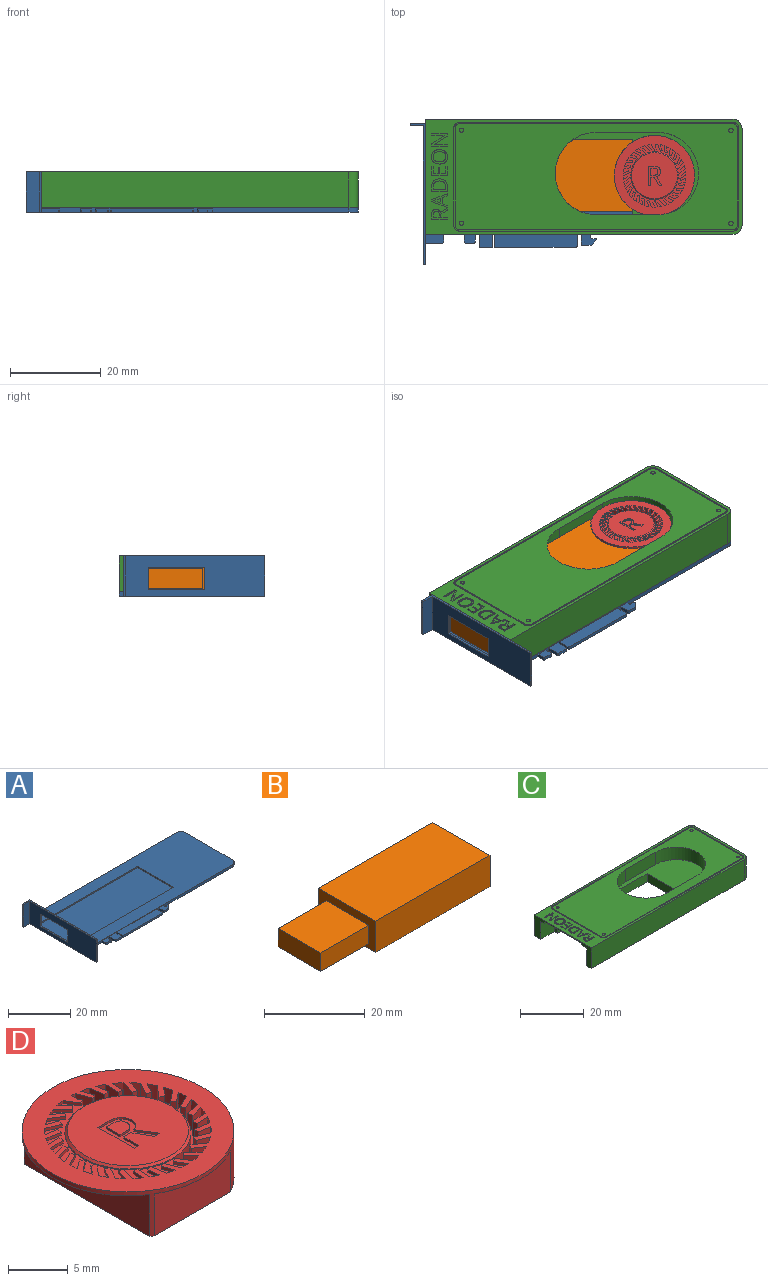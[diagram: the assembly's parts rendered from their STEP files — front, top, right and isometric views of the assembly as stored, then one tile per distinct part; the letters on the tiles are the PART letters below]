
ASSEMBLY  parts=4 mates=3
PART A: 54 faces, bbox 73.4x32.1x8.9 mm
  f0: plane 31.16x8.92mm, normal (1,0,0), area 199.6mm2, adj f2,f6,f7,f21,f22,f39,f40,f43
  f1: plane 30.69x8.92mm, normal (-1,0,0), area 212.9mm2, adj f7,f40,f41,f43,f50,f51,f52,f53
  f2: plane 70x25.41mm, normal (0,0,1), area 1021.4mm2, adj f0,f3,f4,f5,f6,f44,f45,f46
  f3: plane 1x0.96mm, normal (-1,0,0), area 1mm2, adj f2,f5,f7,f39
  f4: plane 21.41x1mm, normal (1,0,0), area 21.4mm2, adj f2,f7,f44,f45
  f5: plane 68x1mm, normal (0,1,0), area 68mm2, adj f2,f3,f7,f44
  f6: plane 68x1mm, normal (0,-1,0), area 46.8mm2, adj f0,f2,f7,f8,f9,f11,f12,f13
  f7: plane 73.36x32.12mm, normal (0,0,-1), area 1872.4mm2, adj f0,f1,f3,f4,f5,f6,f8,f9
  f8: plane 2.68x0.72mm, normal (-1,0,0), area 1.9mm2, adj f6,f7,f11,f37
  f9: plane 2.68x0.72mm, normal (1,0,0), area 1.9mm2, adj f6,f7,f11,f38
  f10: plane 17.82x0.72mm, normal (0,-1,0), area 12.8mm2, adj f7,f11,f37,f38
  f11: plane 18.22x2.88mm, normal (0,0,1), area 52.4mm2, adj f6,f8,f9,f10,f37,f38
  f12: plane 2.68x0.72mm, normal (-1,0,0), area 1.9mm2, adj f6,f7,f15,f36
  f13: plane 2.68x0.72mm, normal (1,0,0), area 1.9mm2, adj f6,f7,f15,f35
  f14: plane 2.48x0.72mm, normal (0,-1,0), area 1.8mm2, adj f7,f15,f35,f36
  f15: plane 2.88x2.88mm, normal (0,0,1), area 8.3mm2, adj f6,f12,f13,f14,f35,f36
  f16: plane 1.72x0.72mm, normal (-1,0,0), area 1.2mm2, adj f6,f7,f19,f33
  f17: plane 1.72x0.72mm, normal (1,0,0), area 1.2mm2, adj f6,f7,f19,f34
  f18: plane 2x0.72mm, normal (0,-1,0), area 1.4mm2, adj f7,f19,f33,f34
  f19: plane 2.4x1.92mm, normal (0,0,1), area 4.6mm2, adj f6,f16,f17,f18,f33,f34
  f20: plane 1.72x0.72mm, normal (1,0,0), area 1.2mm2, adj f6,f7,f22,f32
  f21: plane 3.88x0.72mm, normal (0,-1,0), area 2.8mm2, adj f0,f7,f22,f32
  f22: plane 4.08x1.92mm, normal (0,0,1), area 7.8mm2, adj f0,f6,f20,f21,f32
  f23: plane 2.2x0.72mm, normal (-1,0,0), area 1.6mm2, adj f6,f7,f28,f31
  f24: plane 0.72x0.36mm, normal (1,0,0), area 0.3mm2, adj f6,f7,f28,f30
  f25: plane 0.84x0.72mm, normal (0,1,0), area 0.6mm2, adj f7,f26,f28,f30
  f26: plane 0.72x0.24mm, normal (1,0,0), area 0.2mm2, adj f7,f25,f28,f29
  f27: plane 1.96x0.72mm, normal (0,-1,0), area 1.4mm2, adj f7,f28,f29,f31
  f28: plane 3.36x2.4mm, normal (0,0,1), area 6mm2, adj f6,f23,f24,f25,f26,f27,f29,f30
  f29: plane 1.2x1.2mm, normal (0.71,-0.71,0), area 1.2mm2, adj f7,f26,f27,f28
  f30: cylinder r=0.6mm len=0.72mm, axis (0,0,1), area 0.7mm2, adj f7,f24,f25,f28
  f31: cylinder r=0.2mm len=0.72mm, axis (0,0,-1), area 0.2mm2, adj f7,f23,f27,f28
  f32: cylinder r=0.2mm len=0.72mm, axis (0,0,1), area 0.2mm2, adj f7,f20,f21,f22
  f33: cylinder r=0.2mm len=0.72mm, axis (0,0,-1), area 0.2mm2, adj f7,f16,f18,f19
  f34: cylinder r=0.2mm len=0.72mm, axis (0,0,1), area 0.2mm2, adj f7,f17,f18,f19
  f35: cylinder r=0.2mm len=0.72mm, axis (0,0,1), area 0.2mm2, adj f7,f13,f14,f15
  f36: cylinder r=0.2mm len=0.72mm, axis (0,0,-1), area 0.2mm2, adj f7,f12,f14,f15
  f37: cylinder r=0.2mm len=0.72mm, axis (0,0,-1), area 0.2mm2, adj f7,f8,f10,f11
  f38: cylinder r=0.2mm len=0.72mm, axis (0,0,1), area 0.2mm2, adj f7,f9,f10,f11
  f39: plane 8.92x3.36mm, normal (0,1,0), area 29.9mm2, adj f0,f3,f7,f42,f43
  f40: plane 8.92x0.48mm, normal (0,-1,0), area 4.3mm2, adj f0,f1,f7,f43
  f41: plane 8.92x2.88mm, normal (0,-1,0), area 25.7mm2, adj f1,f7,f42,f43
  f42: plane 8.92x0.48mm, normal (-1,0,0), area 4.3mm2, adj f7,f39,f41,f43
  f43: plane 31.16x3.36mm, normal (0,0,1), area 16.3mm2, adj f0,f1,f39,f40,f41,f42
  f44: cylinder r=2mm len=2mm, axis (0,0,1), area 3.1mm2, adj f2,f4,f5,f7
  f45: cylinder r=2mm len=2mm, axis (0,0,-1), area 3.1mm2, adj f2,f4,f6,f7
  f46: plane 45.8x0.5mm, normal (0,-1,0), area 22.9mm2, adj f0,f2,f48,f49
  f47: plane 45.8x0.5mm, normal (0,1,0), area 22.9mm2, adj f0,f2,f48,f49
  f48: plane 16.5x0.5mm, normal (-1,0,0), area 8.2mm2, adj f2,f46,f47,f49
  f49: plane 45.8x16.5mm, normal (0,0,1), area 755.7mm2, adj f0,f46,f47,f48
  f50: plane 4.9x0.48mm, normal (0,1,0), area 2.3mm2, adj f0,f1,f51,f53
  f51: plane 12.4x0.48mm, normal (0,0,-1), area 5.9mm2, adj f0,f1,f50,f52
  f52: plane 4.9x0.48mm, normal (0,-1,0), area 2.3mm2, adj f0,f1,f51,f53
  f53: plane 12.4x0.48mm, normal (0,0,1), area 5.9mm2, adj f0,f1,f50,f52
PART B: 11 faces, bbox 45.5x16x7.6 mm
  f0: plane 16x7.6mm, normal (1,0,0), area 121.6mm2, adj f1,f3,f4,f5
  f1: plane 32x7.6mm, normal (0,1,0), area 243.2mm2, adj f0,f2,f4,f5
  f2: plane 16x7.6mm, normal (-1,0,0), area 67.6mm2, adj f1,f3,f4,f5,f6,f7,f8,f9
  f3: plane 32x7.6mm, normal (0,-1,0), area 243.2mm2, adj f0,f2,f4,f5
  f4: plane 32x16mm, normal (0,0,1), area 512mm2, adj f0,f1,f2,f3
  f5: plane 32x16mm, normal (0,0,-1), area 512mm2, adj f0,f1,f2,f3
  f6: plane 13.5x4.5mm, normal (0,-1,0), area 60.7mm2, adj f2,f7,f9,f10
  f7: plane 13.5x12mm, normal (0,0,1), area 162mm2, adj f2,f6,f8,f10
  f8: plane 13.5x4.5mm, normal (0,1,0), area 60.7mm2, adj f2,f7,f9,f10
  f9: plane 13.5x12mm, normal (0,0,-1), area 162mm2, adj f2,f6,f8,f10
  f10: plane 12x4.5mm, normal (-1,0,0), area 54mm2, adj f6,f7,f8,f9
PART C: 149 faces, bbox 70x25.4x7.9 mm
  f0: plane 62.41x23.4mm, normal (0,0,1), area 950mm2, adj f19,f20,f21,f22,f23,f24,f25,f26
  f1: plane 16.5x3.12mm, normal (-1,0,0), area 51.5mm2, adj f2,f141,f142,f148
  f2: plane 70x25.41mm, normal (0,0,-1), area 997.9mm2, adj f1,f4,f5,f7,f8,f9,f10,f11
  f3: plane 6x1.46mm, normal (0,0,-1), area 8.7mm2, adj f4,f5,f138,f141
  f4: plane 6.92x1.46mm, normal (-1,0,0), area 10.1mm2, adj f2,f3,f138,f141
  f5: plane 25.41x7.92mm, normal (-1,0,0), area 50.4mm2, adj f2,f3,f6,f8,f9,f137,f138,f139
  f6: plane 70x25.41mm, normal (0,0,1), area 231.5mm2, adj f5,f7,f8,f9,f10,f11,f12,f13
  f7: plane 21.41x7.92mm, normal (1,0,0), area 169.5mm2, adj f2,f6,f10,f11
  f8: plane 68x7.92mm, normal (0,1,0), area 538.4mm2, adj f2,f5,f6,f10
  f9: plane 68x7.92mm, normal (0,-1,0), area 538.4mm2, adj f2,f5,f6,f11
  f10: cylinder r=2mm len=7.92mm, axis (0,0,1), area 24.9mm2, adj f2,f6,f7,f8
  f11: cylinder r=2mm len=7.92mm, axis (0,0,-1), area 24.9mm2, adj f2,f6,f7,f9
  f12: plane 21.41x0.1mm, normal (-1,0,0), area 2.1mm2, adj f6,f13,f27,f28
  f13: cylinder r=1.29mm len=1.29mm, axis (0,0,1), area 0.2mm2, adj f6,f12,f14,f28
  f14: plane 60.42x0.1mm, normal (0,-1,0), area 6mm2, adj f6,f13,f15,f28
  f15: cylinder r=1.29mm len=1.29mm, axis (0,0,1), area 0.2mm2, adj f6,f14,f16,f28
  f16: plane 21.41x0.1mm, normal (1,0,0), area 2.1mm2, adj f6,f15,f17,f28
  f17: cylinder r=1.29mm len=1.29mm, axis (0,0,1), area 0.2mm2, adj f6,f16,f18,f28
  f18: plane 60.42x0.1mm, normal (0,1,0), area 6mm2, adj f6,f17,f27,f28
  f19: cylinder r=0.99mm len=0.99mm, axis (0,0,1), area 0.2mm2, adj f0,f20,f26,f28
  f20: plane 21.41x0.1mm, normal (1,0,0), area 2.1mm2, adj f0,f19,f21,f28
  f21: cylinder r=0.99mm len=0.99mm, axis (0,0,1), area 0.2mm2, adj f0,f20,f22,f28
  f22: plane 60.42x0.1mm, normal (0,-1,0), area 6mm2, adj f0,f21,f23,f28
  f23: cylinder r=0.99mm len=0.99mm, axis (0,0,1), area 0.2mm2, adj f0,f22,f24,f28
  f24: plane 21.41x0.1mm, normal (-1,0,0), area 2.1mm2, adj f0,f23,f25,f28
  f25: cylinder r=0.99mm len=0.99mm, axis (0,0,1), area 0.2mm2, adj f0,f24,f26,f28
  f26: plane 60.42x0.1mm, normal (0,1,0), area 6mm2, adj f0,f19,f25,f28
  f27: cylinder r=1.29mm len=1.29mm, axis (0,0,1), area 0.2mm2, adj f6,f12,f18,f28
  f28: plane 63.01x24mm, normal (0,0,1), area 51.3mm2, adj f12,f13,f14,f15,f16,f17,f18,f19
  f29: cylinder r=0.48mm len=0.96mm, axis (0,0,1), area 0.3mm2, adj f0,f30
  f30: plane 0.96x0.96mm, normal (0,0,1), area 0.7mm2, adj f29
  f31: cylinder r=0.48mm len=0.96mm, axis (0,0,1), area 0.3mm2, adj f0,f32
  f32: plane 0.96x0.96mm, normal (0,0,1), area 0.7mm2, adj f31
  f33: cylinder r=0.48mm len=0.96mm, axis (0,0,1), area 0.3mm2, adj f0,f34
  f34: plane 0.96x0.96mm, normal (0,0,1), area 0.7mm2, adj f33
  f35: cylinder r=0.48mm len=0.96mm, axis (0,0,1), area 0.3mm2, adj f0,f36
  f36: plane 0.96x0.96mm, normal (0,0,1), area 0.7mm2, adj f35
  f37: plane 1.93x0.3mm, normal (-1,0,0), area 0.6mm2, adj f6,f38,f48,f49
  f38: plane 0.38x0.3mm, normal (0,-1,0), area 0.1mm2, adj f6,f37,f39,f49
  f39: plane 1.5x0.3mm, normal (1,0,0), area 0.4mm2, adj f6,f38,f40,f49
  f40: plane 1.24x0.3mm, normal (0,-1,0), area 0.4mm2, adj f6,f39,f41,f49
  f41: plane 1.41x0.3mm, normal (-1,0,0), area 0.4mm2, adj f6,f40,f42,f49
  f42: plane 0.38x0.3mm, normal (0,-1,0), area 0.1mm2, adj f6,f41,f43,f49
  f43: plane 1.41x0.3mm, normal (1,0,0), area 0.4mm2, adj f6,f42,f44,f49
  f44: plane 1.08x0.3mm, normal (0,-1,0), area 0.3mm2, adj f6,f43,f45,f49
  f45: plane 1.5x0.3mm, normal (-1,0,0), area 0.4mm2, adj f6,f44,f46,f49
  f46: plane 0.38x0.3mm, normal (0,-1,0), area 0.1mm2, adj f6,f45,f47,f49
  f47: plane 1.93x0.3mm, normal (1,0,0), area 0.6mm2, adj f6,f46,f48,f49
  f48: plane 3.46x0.3mm, normal (0,1,0), area 1mm2, adj f6,f37,f47,f49
  f49: plane 3.46x1.93mm, normal (0,0,1), area 3.2mm2, adj f37,f38,f39,f40,f41,f42,f43,f44
  f50: extruded ~1.05x0.3mm, area 0.3mm2, adj f51,f65,f66,f134
  f51: extruded ~1.04x0.3mm, area 0.3mm2, adj f50,f52,f66,f134
  f52: extruded ~0.85x0.36mm, area 0.3mm2, adj f51,f53,f66,f134
  f53: extruded ~0.84x0.35mm, area 0.3mm2, adj f52,f54,f66,f134
  f54: extruded ~1.04x0.3mm, area 0.3mm2, adj f53,f55,f66,f134
  f55: extruded ~1.05x0.3mm, area 0.3mm2, adj f54,f56,f66,f134
  f56: extruded ~0.85x0.36mm, area 0.3mm2, adj f55,f65,f66,f134
  f57: extruded ~1.31x0.42mm, area 0.4mm2, adj f6,f58,f64,f66
  f58: extruded ~1.31x0.42mm, area 0.4mm2, adj f6,f57,f59,f66
  f59: extruded ~1.17x0.47mm, area 0.4mm2, adj f6,f58,f60,f66
  f60: extruded ~1.19x0.47mm, area 0.4mm2, adj f6,f59,f61,f66
  f61: extruded ~1.31x0.42mm, area 0.4mm2, adj f6,f60,f62,f66
  f62: extruded ~1.32x0.42mm, area 0.4mm2, adj f6,f61,f63,f66
  f63: extruded ~1.18x0.47mm, area 0.4mm2, adj f6,f62,f64,f66
  f64: extruded ~1.18x0.48mm, area 0.4mm2, adj f6,f57,f63,f66
  f65: extruded ~0.85x0.36mm, area 0.3mm2, adj f50,f56,f66,f134
  f66: plane 3.56x3.19mm, normal (0,0,1), area 4mm2, adj f50,f51,f52,f53,f54,f55,f56,f57
  f67: plane 0.51x0.3mm, normal (-1,0,0), area 0.2mm2, adj f6,f68,f84,f85
  f68: plane 3.46x0.3mm, normal (0,-1,0), area 1mm2, adj f6,f67,f69,f85
  f69: plane 0.41x0.3mm, normal (1,0,0), area 0.1mm2, adj f6,f68,f70,f85
  f70: plane 1.95x0.3mm, normal (0,1,0), area 0.6mm2, adj f6,f69,f71,f85
  f71: extruded ~0.51x0.3mm, area 0.2mm2, adj f6,f70,f72,f85
  f72: extruded ~0.41x0.3mm, area 0.1mm2, adj f6,f71,f73,f85
  f73: plane 0.3x0.02mm, normal (1,0,0), area 0mm2, adj f6,f72,f74,f85
  f74: plane 0.94x0.6mm, normal (0.54,-0.84,0), area 0.3mm2, adj f6,f73,f75,f85
  f75: plane 1.76x1.14mm, normal (0.54,-0.84,0), area 0.6mm2, adj f6,f74,f76,f85
  f76: plane 0.3x0.17mm, normal (0.53,-0.85,0), area 0.1mm2, adj f6,f75,f77,f85
  f77: plane 0.5x0.3mm, normal (1,0,0), area 0.2mm2, adj f6,f76,f78,f85
  f78: plane 3.46x0.3mm, normal (0,1,0), area 1mm2, adj f6,f77,f79,f85
  f79: plane 0.4x0.3mm, normal (-1,0,0), area 0.1mm2, adj f6,f78,f80,f85
  f80: plane 1.93x0.3mm, normal (0,-1,0), area 0.6mm2, adj f6,f79,f81,f85
  f81: extruded ~0.75x0.3mm, area 0.2mm2, adj f6,f80,f82,f85
  f82: plane 0.3x0.19mm, normal (0.06,-1,0), area 0.1mm2, adj f6,f81,f83,f85
  f83: plane 0.3x0.02mm, normal (-1,0,0), area 0mm2, adj f6,f82,f84,f85
  f84: plane 2.87x1.85mm, normal (-0.54,0.84,0), area 1mm2, adj f6,f67,f83,f85
  f85: plane 3.46x2.74mm, normal (0,0,1), area 4.3mm2, adj f67,f68,f69,f70,f71,f72,f73,f74
  f86: plane 1.43x0.3mm, normal (0,-1,0), area 0.4mm2, adj f6,f87,f103,f104
  f87: plane 0.69x0.3mm, normal (-1,0,0), area 0.2mm2, adj f6,f86,f88,f104
  f88: plane 1.43x0.84mm, normal (-0.51,0.86,0), area 0.5mm2, adj f6,f87,f89,f104
  f89: plane 0.51x0.3mm, normal (-1,0,0), area 0.2mm2, adj f6,f88,f90,f104
  f90: plane 1.55x0.95mm, normal (0.52,-0.85,0), area 0.5mm2, adj f6,f89,f91,f104
  f91: extruded ~0.93x0.69mm, area 0.4mm2, adj f6,f90,f92,f104
  f92: extruded ~0.74x0.31mm, area 0.2mm2, adj f6,f91,f93,f104
  f93: extruded ~0.95x0.3mm, area 0.3mm2, adj f6,f92,f94,f104
  f94: plane 0.95x0.3mm, normal (1,0,0), area 0.3mm2, adj f6,f93,f95,f104
  f95: plane 3.46x0.3mm, normal (0,1,0), area 1mm2, adj f6,f94,f103,f104
  f96: plane 0.52x0.3mm, normal (1,0,0), area 0.2mm2, adj f97,f102,f104,f105
  f97: plane 1.29x0.3mm, normal (0,-1,0), area 0.4mm2, adj f96,f98,f104,f105
  f98: plane 0.49x0.3mm, normal (-1,0,0), area 0.1mm2, adj f97,f99,f104,f105
  f99: extruded ~0.64x0.3mm, area 0.2mm2, adj f98,f100,f104,f105
  f100: extruded ~0.48x0.3mm, area 0.2mm2, adj f99,f101,f104,f105
  f101: extruded ~0.49x0.3mm, area 0.2mm2, adj f100,f102,f104,f105
  f102: extruded ~0.62x0.3mm, area 0.2mm2, adj f96,f101,f104,f105
  f103: plane 0.44x0.3mm, normal (-1,0,0), area 0.1mm2, adj f6,f86,f95,f104
  f104: plane 3.46x2.47mm, normal (0,0,1), area 3.8mm2, adj f86,f87,f88,f89,f90,f91,f92,f93
  f105: plane 1.33x1.29mm, normal (0,0,1), area 1.5mm2, adj f96,f97,f98,f99,f100,f101,f102
  f106: plane 1.05x0.39mm, normal (-0.35,0.94,0), area 0.3mm2, adj f107,f118,f119,f135
  f107: plane 1.1x0.3mm, normal (1,0,0), area 0.3mm2, adj f106,f108,f119,f135
  f108: plane 1.05x0.39mm, normal (-0.35,-0.94,0), area 0.3mm2, adj f107,f109,f119,f135
  f109: extruded ~0.52x0.3mm, area 0.2mm2, adj f108,f118,f119,f135
  f110: plane 1.07x0.42mm, normal (-0.36,0.93,0), area 0.3mm2, adj f6,f111,f117,f119
  f111: plane 0.45x0.3mm, normal (-1,0,0), area 0.1mm2, adj f6,f110,f112,f119
  f112: plane 3.47x1.35mm, normal (0.36,-0.93,0), area 1.1mm2, adj f6,f111,f113,f119
  f113: plane 0.39x0.3mm, normal (1,0,0), area 0.1mm2, adj f6,f112,f114,f119
  f114: plane 3.47x1.35mm, normal (0.36,0.93,0), area 1.1mm2, adj f6,f113,f115,f119
  f115: plane 0.44x0.3mm, normal (-1,0,0), area 0.1mm2, adj f6,f114,f116,f119
  f116: plane 1.07x0.41mm, normal (-0.36,-0.93,0), area 0.3mm2, adj f6,f115,f117,f119
  f117: plane 1.37x0.3mm, normal (-1,0,0), area 0.4mm2, adj f6,f110,f116,f119
  f118: plane 0.52x0.3mm, normal (-0.3,0.95,0), area 0.2mm2, adj f106,f109,f119,f135
  f119: plane 3.47x3.09mm, normal (0,0,1), area 3.3mm2, adj f106,f107,f108,f109,f110,f111,f112,f113
  f120: extruded ~1x0.33mm, area 0.3mm2, adj f121,f132,f133,f136
  f121: extruded ~1.41x1.37mm, area 0.7mm2, adj f120,f122,f133,f136
  f122: plane 0.47x0.3mm, normal (1,0,0), area 0.1mm2, adj f121,f123,f133,f136
  f123: plane 2.71x0.3mm, normal (0,-1,0), area 0.8mm2, adj f122,f124,f133,f136
  f124: plane 0.57x0.3mm, normal (-1,0,0), area 0.2mm2, adj f123,f132,f133,f136
  f125: extruded ~1.31x0.47mm, area 0.4mm2, adj f6,f126,f131,f133
  f126: extruded ~1.25x0.45mm, area 0.4mm2, adj f6,f125,f127,f133
  f127: extruded ~1.26x0.44mm, area 0.4mm2, adj f6,f126,f128,f133
  f128: plane 1.06x0.3mm, normal (1,0,0), area 0.3mm2, adj f6,f127,f129,f133
  f129: plane 3.46x0.3mm, normal (0,1,0), area 1mm2, adj f6,f128,f130,f133
  f130: plane 0.96x0.3mm, normal (-1,0,0), area 0.3mm2, adj f6,f129,f131,f133
  f131: extruded ~1.34x0.45mm, area 0.4mm2, adj f6,f125,f130,f133
  f132: extruded ~0.98x0.34mm, area 0.3mm2, adj f120,f124,f133,f136
  f133: plane 3.46x2.77mm, normal (0,0,1), area 4mm2, adj f120,f121,f122,f123,f124,f125,f126,f127
  f134: plane 2.8x2.27mm, normal (0,0,1), area 5.3mm2, adj f50,f51,f52,f53,f54,f55,f56,f65
  f135: plane 1.57x1.1mm, normal (0,0,1), area 0.8mm2, adj f106,f107,f108,f109,f118
  f136: plane 2.71x1.88mm, normal (0,0,1), area 4.5mm2, adj f120,f121,f122,f123,f124,f132
  f137: plane 6x2.46mm, normal (0,0,-1), area 14.7mm2, adj f5,f139,f140,f142
  f138: plane 6.92x6mm, normal (0,-1,0), area 41.5mm2, adj f2,f3,f4,f5
  f139: plane 6.92x6mm, normal (0,1,0), area 41.5mm2, adj f2,f5,f137,f140
  f140: plane 6.92x2.46mm, normal (-1,0,0), area 17mm2, adj f2,f137,f139,f142
  f141: plane 45.8x7.5mm, normal (0,-1,0), area 244.6mm2, adj f1,f2,f3,f4,f5,f143,f145,f148
  f142: plane 45.8x7.5mm, normal (0,1,0), area 260mm2, adj f1,f2,f5,f137,f140,f143,f145,f148
  f143: plane 36.22x16.5mm, normal (0,0,-1), area 499.1mm2, adj f5,f141,f142,f145
  f144: plane 13.49x4.79mm, normal (0,-1,0), area 64.7mm2, adj f0,f145,f147,f148
  f145: cylinder r=9.11mm len=18.22mm, axis (0,0,1), area 42.8mm2, adj f0,f141,f142,f143,f144,f146,f148
  f146: plane 13.49x4.79mm, normal (0,1,0), area 64.7mm2, adj f0,f145,f147,f148
  f147: cylinder r=9.11mm len=18.22mm, axis (0,0,1), area 137.2mm2, adj f0,f144,f146,f148
  f148: plane 27.73x18.22mm, normal (0,0,1), area 250mm2, adj f1,f141,f142,f144,f145,f146,f147
PART D: 157 faces, bbox 17.7x17.7x4.7 mm
  f0: plane 10.15x10.15mm, normal (0,0,1), area 72.7mm2, adj f136,f143,f144,f145,f146,f147,f148,f149
  f1: cylinder r=8.87mm len=17.74mm, axis (0,0,-1), area 105.5mm2, adj f2,f3,f4,f5,f6,f7,f8,f9
  f2: plane 15.28x13.74mm, normal (0,0,-1), area 190.4mm2, adj f1,f4,f6,f9
  f3: plane 17.74x17.74mm, normal (0,0,1), area 117.1mm2, adj f1,f10,f11,f12,f13,f14,f15,f16
  f4: plane 9.01x4.29mm, normal (0,1,0), area 38.6mm2, adj f1,f2,f5
  f5: plane 9.01x1.23mm, normal (0,0,-1), area 7.5mm2, adj f1,f4
  f6: plane 14.83x4.29mm, normal (-1,0,0), area 63.6mm2, adj f1,f2,f7
  f7: plane 14.83x4mm, normal (0,0,-1), area 41.8mm2, adj f1,f6
  f8: plane 9.01x1.23mm, normal (0,0,-1), area 7.5mm2, adj f1,f9
  f9: plane 9.01x4.29mm, normal (0,-1,0), area 38.6mm2, adj f1,f2,f8
  f10: plane 1.5x0.42mm, normal (0.53,-0.85,0), area 0.5mm2, adj f3,f11,f131,f132,f133,f135
  f11: plane 1.33x0.83mm, normal (-0.85,-0.53,0), area 0.5mm2, adj f3,f10,f12,f132
  f12: cylinder r=6.95mm len=0.87mm, axis (0,0,1), area 0.3mm2, adj f3,f11,f13,f132
  f13: plane 0.93x0.91mm, normal (0.72,0.7,0), area 0.4mm2, adj f3,f12,f14,f132
  f14: plane 0.36x0.35mm, normal (0.7,-0.72,0), area 0.2mm2, adj f3,f13,f15,f132
  f15: plane 1.12x1.09mm, normal (-0.72,-0.7,0), area 0.5mm2, adj f3,f14,f16,f132
  f16: cylinder r=6.95mm len=0.82mm, axis (0,0,1), area 0.3mm2, adj f3,f15,f17,f132
  f17: plane 1.08x0.72mm, normal (0.56,0.83,0), area 0.4mm2, adj f3,f16,f18,f132
  f18: plane 0.42x0.3mm, normal (0.83,-0.56,0), area 0.2mm2, adj f3,f17,f19,f132
  f19: plane 1.3x0.87mm, normal (-0.56,-0.83,0), area 0.5mm2, adj f3,f18,f20,f132
  f20: cylinder r=6.95mm len=0.74mm, axis (0,0,1), area 0.3mm2, adj f3,f19,f21,f132
  f21: plane 1.21x0.48mm, normal (0.37,0.93,0), area 0.4mm2, adj f3,f20,f22,f132
  f22: plane 0.46x0.3mm, normal (0.93,-0.37,0), area 0.1mm2, adj f3,f21,f23,f132
  f23: plane 1.46x0.58mm, normal (-0.37,-0.93,0), area 0.5mm2, adj f3,f22,f24,f132
  f24: cylinder r=6.95mm len=0.64mm, axis (0,0,1), area 0.3mm2, adj f3,f23,f25,f132
  f25: plane 1.28x0.3mm, normal (0.17,0.99,0), area 0.4mm2, adj f3,f24,f26,f132
  f26: plane 0.49x0.3mm, normal (0.99,-0.17,0), area 0.1mm2, adj f3,f25,f27,f132
  f27: plane 1.55x0.3mm, normal (-0.17,-0.99,0), area 0.5mm2, adj f3,f26,f28,f132
  f28: cylinder r=6.95mm len=0.75mm, axis (0,0,1), area 0.3mm2, adj f3,f27,f29,f132
  f29: plane 1.3x0.3mm, normal (-0.04,1,0), area 0.4mm2, adj f3,f28,f30,f132
  f30: plane 0.5x0.3mm, normal (1,0.04,0), area 0.2mm2, adj f3,f29,f31,f132
  f31: plane 1.57x0.3mm, normal (0.04,-1,0), area 0.5mm2, adj f3,f30,f32,f132
  f32: cylinder r=6.95mm len=0.83mm, axis (0,0,1), area 0.3mm2, adj f3,f31,f33,f132
  f33: plane 1.26x0.32mm, normal (-0.24,0.97,0), area 0.4mm2, adj f3,f32,f34,f132
  f34: plane 0.48x0.3mm, normal (0.97,0.24,0), area 0.2mm2, adj f3,f33,f35,f132
  f35: plane 1.52x0.38mm, normal (0.24,-0.97,0), area 0.5mm2, adj f3,f34,f36,f132
  f36: cylinder r=6.95mm len=0.88mm, axis (0,0,1), area 0.3mm2, adj f3,f35,f37,f132
  f37: plane 1.17x0.57mm, normal (-0.44,0.9,0), area 0.4mm2, adj f3,f36,f38,f132
  f38: plane 0.45x0.3mm, normal (0.9,0.44,0), area 0.2mm2, adj f3,f37,f39,f132
  f39: plane 1.41x0.69mm, normal (0.44,-0.9,0), area 0.5mm2, adj f3,f38,f40,f132
  f40: cylinder r=6.95mm len=0.89mm, axis (0,0,1), area 0.3mm2, adj f3,f39,f41,f132
  f41: plane 1.02x0.8mm, normal (-0.62,0.79,0), area 0.4mm2, adj f3,f40,f42,f132
  f42: plane 0.39x0.31mm, normal (0.79,0.62,0), area 0.2mm2, adj f3,f41,f43,f132
  f43: plane 1.23x0.97mm, normal (0.62,-0.79,0), area 0.5mm2, adj f3,f42,f44,f132
  f44: cylinder r=6.95mm len=0.85mm, axis (0,0,1), area 0.3mm2, adj f3,f43,f45,f132
  f45: plane 1x0.83mm, normal (-0.77,0.64,0), area 0.4mm2, adj f3,f44,f46,f132
  f46: plane 0.38x0.32mm, normal (0.64,0.77,0), area 0.1mm2, adj f3,f45,f47,f132
  f47: plane 1.2x1mm, normal (0.77,-0.64,0), area 0.5mm2, adj f3,f46,f48,f132
  f48: cylinder r=6.95mm len=0.78mm, axis (0,0,1), area 0.3mm2, adj f3,f47,f49,f132
  f49: plane 1.15x0.61mm, normal (-0.88,0.47,0), area 0.4mm2, adj f3,f48,f50,f132
  f50: plane 0.44x0.3mm, normal (0.47,0.88,0), area 0.2mm2, adj f3,f49,f51,f132
  f51: plane 1.39x0.73mm, normal (0.88,-0.47,0), area 0.5mm2, adj f3,f50,f52,f132
  f52: cylinder r=6.95mm len=0.68mm, axis (0,0,1), area 0.3mm2, adj f3,f51,f53,f132
  f53: plane 1.25x0.35mm, normal (-0.96,0.27,0), area 0.4mm2, adj f3,f52,f54,f132
  f54: plane 0.48x0.3mm, normal (0.27,0.96,0), area 0.2mm2, adj f3,f53,f55,f132
  f55: plane 1.51x0.43mm, normal (0.96,-0.27,0), area 0.5mm2, adj f3,f54,f56,f132
  f56: cylinder r=6.95mm len=0.7mm, axis (0,0,1), area 0.3mm2, adj f3,f55,f57,f132
  f57: plane 1.3x0.3mm, normal (-1,0.07,0), area 0.4mm2, adj f3,f56,f58,f132
  f58: plane 0.5x0.3mm, normal (0.07,1,0), area 0.2mm2, adj f3,f57,f59,f132
  f59: plane 1.56x0.3mm, normal (1,-0.07,0), area 0.5mm2, adj f3,f58,f60,f132
  f60: cylinder r=6.95mm len=0.8mm, axis (0,0,1), area 0.3mm2, adj f3,f59,f61,f132
  f61: plane 1.29x0.3mm, normal (-0.99,-0.14,0), area 0.4mm2, adj f3,f60,f62,f132
  f62: plane 0.5x0.3mm, normal (-0.14,0.99,0), area 0.1mm2, adj f3,f61,f63,f132
  f63: plane 1.55x0.3mm, normal (0.99,0.14,0), area 0.5mm2, adj f3,f62,f64,f132
  f64: cylinder r=6.95mm len=0.86mm, axis (0,0,1), area 0.3mm2, adj f3,f63,f65,f132
  f65: plane 1.22x0.45mm, normal (-0.94,-0.34,0), area 0.4mm2, adj f3,f64,f66,f132
  f66: plane 0.47x0.3mm, normal (-0.34,0.94,0), area 0.1mm2, adj f3,f65,f67,f132
  f67: plane 1.47x0.54mm, normal (0.94,0.34,0), area 0.5mm2, adj f3,f66,f68,f132
  f68: cylinder r=6.95mm len=0.89mm, axis (0,0,1), area 0.3mm2, adj f3,f67,f69,f132
  f69: plane 1.1x0.69mm, normal (-0.85,-0.53,0), area 0.4mm2, adj f3,f68,f70,f132
  f70: plane 0.42x0.3mm, normal (-0.53,0.85,0), area 0.1mm2, adj f3,f69,f71,f132
  f71: plane 1.5x1.33mm, normal (0.85,0.53,0), area 1.6mm2, adj f3,f70,f72,f132,f134,f135
  f72: cylinder r=6.95mm len=1.5mm, axis (0,0,1), area 1.3mm2, adj f3,f71,f73,f135
  f73: plane 1.5x0.93mm, normal (-0.72,-0.7,0), area 1.9mm2, adj f3,f72,f74,f135
  f74: plane 1.5x0.36mm, normal (-0.7,0.72,0), area 0.8mm2, adj f3,f73,f75,f135
  f75: plane 1.5x1.12mm, normal (0.72,0.7,0), area 2.4mm2, adj f3,f74,f76,f135
  f76: cylinder r=6.95mm len=1.5mm, axis (0,0,1), area 1.3mm2, adj f3,f75,f77,f135
  f77: plane 1.5x1.08mm, normal (-0.56,-0.83,0), area 1.9mm2, adj f3,f76,f78,f135
  f78: plane 1.5x0.42mm, normal (-0.83,0.56,0), area 0.8mm2, adj f3,f77,f79,f135
  f79: plane 1.5x1.3mm, normal (0.56,0.83,0), area 2.4mm2, adj f3,f78,f80,f135
  f80: cylinder r=6.95mm len=1.5mm, axis (0,0,1), area 1.3mm2, adj f3,f79,f81,f135
  f81: plane 1.5x1.21mm, normal (-0.37,-0.93,0), area 2mm2, adj f3,f80,f82,f135
  f82: plane 1.5x0.46mm, normal (-0.93,0.37,0), area 0.7mm2, adj f3,f81,f83,f135
  f83: plane 1.5x1.46mm, normal (0.37,0.93,0), area 2.4mm2, adj f3,f82,f84,f135
  f84: cylinder r=6.95mm len=1.5mm, axis (0,0,1), area 1.3mm2, adj f3,f83,f85,f135
  f85: plane 1.5x1.28mm, normal (-0.17,-0.99,0), area 2mm2, adj f3,f84,f86,f135
  f86: plane 1.5x0.49mm, normal (-0.99,0.17,0), area 0.7mm2, adj f3,f85,f87,f135
  f87: plane 1.55x1.5mm, normal (0.17,0.99,0), area 2.4mm2, adj f3,f86,f88,f135
  f88: cylinder r=6.95mm len=1.5mm, axis (0,0,1), area 1.3mm2, adj f3,f87,f89,f135
  f89: plane 1.5x1.3mm, normal (0.04,-1,0), area 2mm2, adj f3,f88,f90,f135
  f90: plane 1.5x0.5mm, normal (-1,-0.04,0), area 0.8mm2, adj f3,f89,f91,f135
  f91: plane 1.57x1.5mm, normal (-0.04,1,0), area 2.4mm2, adj f3,f90,f92,f135
  f92: cylinder r=6.95mm len=1.5mm, axis (0,0,1), area 1.3mm2, adj f3,f91,f93,f135
  f93: plane 1.5x1.26mm, normal (0.24,-0.97,0), area 2mm2, adj f3,f92,f94,f135
  f94: plane 1.5x0.48mm, normal (-0.97,-0.24,0), area 0.8mm2, adj f3,f93,f95,f135
  f95: plane 1.52x1.5mm, normal (-0.24,0.97,0), area 2.4mm2, adj f3,f94,f96,f135
  f96: cylinder r=6.95mm len=1.5mm, axis (0,0,1), area 1.3mm2, adj f3,f95,f97,f135
  f97: plane 1.5x1.17mm, normal (0.44,-0.9,0), area 1.9mm2, adj f3,f96,f98,f135
  f98: plane 1.5x0.45mm, normal (-0.9,-0.44,0), area 0.8mm2, adj f3,f97,f99,f135
  f99: plane 1.5x1.41mm, normal (-0.44,0.9,0), area 2.4mm2, adj f3,f98,f100,f135
  f100: cylinder r=6.95mm len=1.5mm, axis (0,0,1), area 1.3mm2, adj f3,f99,f101,f135
  f101: plane 1.5x1.02mm, normal (0.62,-0.79,0), area 1.9mm2, adj f3,f100,f102,f135
  f102: plane 1.5x0.39mm, normal (-0.79,-0.62,0), area 0.8mm2, adj f3,f101,f103,f135
  f103: plane 1.5x1.23mm, normal (-0.62,0.79,0), area 2.4mm2, adj f3,f102,f104,f135
  f104: cylinder r=6.95mm len=1.5mm, axis (0,0,1), area 1.3mm2, adj f3,f103,f105,f135
  f105: plane 1.5x1mm, normal (0.77,-0.64,0), area 1.9mm2, adj f3,f104,f106,f135
  f106: plane 1.5x0.38mm, normal (-0.64,-0.77,0), area 0.7mm2, adj f3,f105,f107,f135
  f107: plane 1.5x1.2mm, normal (-0.77,0.64,0), area 2.4mm2, adj f3,f106,f108,f135
  f108: cylinder r=6.95mm len=1.5mm, axis (0,0,1), area 1.3mm2, adj f3,f107,f109,f135
  f109: plane 1.5x1.15mm, normal (0.88,-0.47,0), area 2mm2, adj f3,f108,f110,f135
  f110: plane 1.5x0.44mm, normal (-0.47,-0.88,0), area 0.8mm2, adj f3,f109,f111,f135
  f111: plane 1.5x1.39mm, normal (-0.88,0.47,0), area 2.4mm2, adj f3,f110,f112,f135
  f112: cylinder r=6.95mm len=1.5mm, axis (0,0,1), area 1.3mm2, adj f3,f111,f113,f135
  f113: plane 1.5x1.25mm, normal (0.96,-0.27,0), area 1.9mm2, adj f3,f112,f114,f135
  f114: plane 1.5x0.48mm, normal (-0.27,-0.96,0), area 0.8mm2, adj f3,f113,f115,f135
  f115: plane 1.51x1.5mm, normal (-0.96,0.27,0), area 2.4mm2, adj f3,f114,f116,f135
  f116: cylinder r=6.95mm len=1.5mm, axis (0,0,1), area 1.3mm2, adj f3,f115,f117,f135
  f117: plane 1.5x1.3mm, normal (1,-0.07,0), area 1.9mm2, adj f3,f116,f118,f135
  f118: plane 1.5x0.5mm, normal (-0.07,-1,0), area 0.8mm2, adj f3,f117,f119,f135
  f119: plane 1.56x1.5mm, normal (-1,0.07,0), area 2.4mm2, adj f3,f118,f120,f135
  f120: cylinder r=6.95mm len=1.5mm, axis (0,0,1), area 1.3mm2, adj f3,f119,f121,f135
  f121: plane 1.5x1.29mm, normal (0.99,0.14,0), area 2mm2, adj f3,f120,f122,f135
  f122: plane 1.5x0.5mm, normal (0.14,-0.99,0), area 0.7mm2, adj f3,f121,f123,f135
  f123: plane 1.55x1.5mm, normal (-0.99,-0.14,0), area 2.4mm2, adj f3,f122,f124,f135
  f124: cylinder r=6.95mm len=1.5mm, axis (0,0,1), area 1.3mm2, adj f3,f123,f125,f135
  f125: plane 1.5x1.22mm, normal (0.94,0.34,0), area 2mm2, adj f3,f124,f126,f135
  f126: plane 1.5x0.47mm, normal (0.34,-0.94,0), area 0.7mm2, adj f3,f125,f127,f135
  f127: plane 1.5x1.47mm, normal (-0.94,-0.34,0), area 2.4mm2, adj f3,f126,f128,f135
  f128: cylinder r=6.95mm len=1.5mm, axis (0,0,1), area 0.7mm2, adj f3,f127,f129,f135
  f129: plane 1.5x0.71mm, normal (1,0,0), area 1.1mm2, adj f3,f128,f131,f135
  f130: cylinder r=5.27mm len=10.55mm, axis (0,0,1), area 22.6mm2, adj f132,f133,f134,f135,f136
  f131: plane 1.5x0.38mm, normal (0.85,0.53,0), area 0.7mm2, adj f3,f10,f129,f135
  f132: plane 13.86x7.2mm, normal (0,0,1), area 21.7mm2, adj f10,f11,f12,f13,f14,f15,f16,f17
  f133: plane 1.2x0.43mm, normal (1,0,0), area 0.5mm2, adj f10,f130,f132,f135
  f134: plane 1.2x0.82mm, normal (1,0,0), area 1mm2, adj f71,f130,f132,f135
  f135: plane 13.86x6.7mm, normal (0,0,1), area 21mm2, adj f10,f71,f72,f73,f74,f75,f76,f77
  f136: cone r=5.07mm half-angle=45deg, axis (0,0,-1), area 9.2mm2, adj f0,f130
  f137: extruded ~0.76x0.21mm, area 0.2mm2, adj f138,f154,f155,f156
  f138: plane 0.64x0.2mm, normal (0,-1,0), area 0.1mm2, adj f137,f139,f155,f156
  f139: plane 1.59x0.2mm, normal (-1,0,0), area 0.3mm2, adj f138,f140,f155,f156
  f140: plane 0.61x0.2mm, normal (0,1,0), area 0.1mm2, adj f139,f141,f155,f156
  f141: extruded ~0.79x0.2mm, area 0.2mm2, adj f140,f142,f155,f156
  f142: extruded ~0.59x0.24mm, area 0.1mm2, adj f141,f154,f155,f156
  f143: plane 0.85x0.2mm, normal (0,1,0), area 0.2mm2, adj f0,f144,f153,f155
  f144: plane 1.77x1.04mm, normal (0.86,0.51,0), area 0.4mm2, adj f0,f143,f145,f155
  f145: plane 0.63x0.2mm, normal (0,1,0), area 0.1mm2, adj f0,f144,f146,f155
  f146: plane 1.92x1.17mm, normal (-0.85,-0.52,0), area 0.4mm2, adj f0,f145,f147,f155
  f147: extruded ~1.15x0.86mm, area 0.3mm2, adj f0,f146,f148,f155
  f148: extruded ~0.91x0.38mm, area 0.2mm2, adj f0,f147,f149,f155
  f149: extruded ~1.18x0.3mm, area 0.2mm2, adj f0,f148,f150,f155
  f150: plane 1.18x0.2mm, normal (0,-1,0), area 0.2mm2, adj f0,f149,f151,f155
  f151: plane 4.28x0.2mm, normal (1,0,0), area 0.9mm2, adj f0,f150,f152,f155
  f152: plane 0.54x0.2mm, normal (0,1,0), area 0.1mm2, adj f0,f151,f153,f155
  f153: plane 1.77x0.2mm, normal (-1,0,0), area 0.4mm2, adj f0,f143,f152,f155
  f154: extruded ~0.61x0.24mm, area 0.1mm2, adj f137,f142,f155,f156
  f155: plane 4.28x3.05mm, normal (0,0,1), area 5.9mm2, adj f137,f138,f139,f140,f141,f142,f143,f144
  f156: plane 1.64x1.59mm, normal (0,0,1), area 2.4mm2, adj f137,f138,f139,f140,f141,f142,f154
PLACE A t=(33.17,35.6,17.36)mm
PLACE B t=(27.97,35.85,17.86)mm
PLACE C t=(33.17,35.6,17.36)mm
PLACE D t=(48.84,35.85,21.17)mm
MATE parallel B.f0 <-> A.f48  axis (1,0,0) through (43.97,43.85,17.86)mm
MATE parallel D.f7 <-> B.f4  axis (0,0,-1) through (43.97,35.85,25.46)mm
MATE parallel C.f11 <-> A.f45  axis (0,0,-1) through (66.17,24.9,18.36)mm
